# Revit family: Lighting_Desk-Table_Nordlux_Darci-Table
name_source: partatom
category: Lighting Fixtures
revit_build: Autodesk Revit 2018 (Build: 20170223_1515(x64)
units: mm (PartAtom-declared; Revit-internal decimal feet)

## family parameters
Always vertical = No
Cut with Voids When Loaded = No
Light Source = No
OmniClass Number = 23.35.47.11
OmniClass Title = Lighting Fixtures
Part Type = Normal
Room Calculation Point = No
Round Connector Dimension = Use Diameter
Shared = No
Work Plane-Based = Yes

## types (1)
- ART - (2120565003)
    Apparent Load = 5 VA
    BIMobject category = Desk & Table
    Beam angle = 121.80°
    Body material = Nordlux - Metal - Black
    CQS = 80.7
    CRI / Ra = 80.3
    Default Elevation = 1219.2 mm  [stored 4 ft]
    Description = With a cool and industrial design, the Darci series by Bjørn + Balle is both a highly functional and aesthetic addition to your home. Perfect next to your sofa, armchair or any other place in your home that needs a stylish and functional light. The beautifully curved lamp head is easily adjusted whether you need it for reading, working or just adding the right ambience to the room. High quality materials with a satin soft, matt surface radiate a modern and streamlined look.
    Design country = Denmark
    EANNumber = 2120565003
    Edition number = 1
    Flicker frequency = 100 Hz
    IFC Classification = Light Fixture
    Installation instructions = https://asset.productmarketingcloud.com
    Light bulb material = Nordlux - Glass - Glass transparent
    Light bulb thread material = Nordlux - Metal - Black
    Manufacturer = Nordlux
    Manufacturer country = China
    Manufacturer name = Nordlux
    Material main = Metal
    Material secondary = Plastic
    Model = Darci table
    NominalVoltage = 230 V
    OmniClass Code = 23-35 47 11
    OmniClass Description = Lighting Fixtures
    Peak [cd] = 109
    Power factor = 0.53
    Product Guid = ba566e29-9b6e-4a63-a1ef-06c148b99e9b
    Product SKU = Darci-Table
    Product data url = https://bimobject.com
    Product family = Lighting
    Product group = Table
    Product name = Darci Table
    Product url = https://nordlux.com
    QR code = https://bimobject.com
    Shade inner material = Nordlux - Metal - White RAL 9016
    Shade material = Nordlux - Metal - Black
    TM30 Rf = 83.3
    TM30 Rg = 91.4
    URL = www.nordlux.com
    Weight Net (Kg) = 2,7
    Youtube clip = https://www.youtube.com

note: [stored X ft] marks values corroborated as IEEE doubles in the binary element streams (Revit-internal decimal feet)

## geometry (parser evidence)
native form markers: Sweep x12
no freeform markers — native parametric forms only
